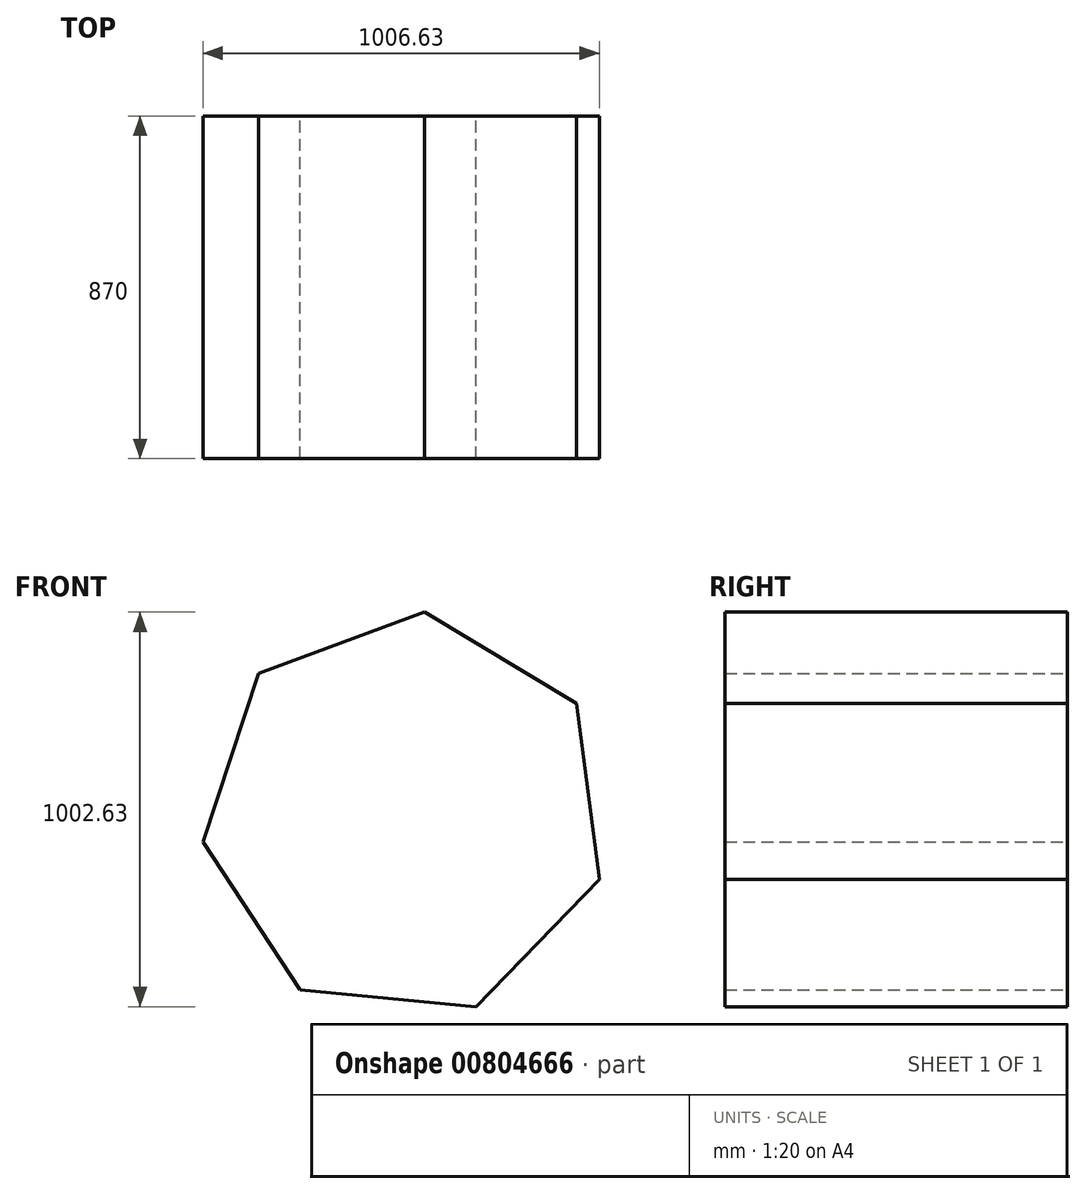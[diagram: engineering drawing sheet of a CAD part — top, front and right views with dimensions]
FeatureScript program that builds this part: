
annotation { "Feature Type Name" : "Feature", "Feature Type Description" : "" }
export const myFeature = defineFeature(function(context is Context, id is Id, definition is map)
    precondition{}
    {
        {
            var Q0;
            Q0=qCreatedBy(makeId("Front.planeOp"),FACE);
            var sketch = newSketch(context, id + "F0", { "sketchPlane" : qUnion([Q0])});
            skCircle(sketch, "E0.cCircle", {"center": v(0, -30.66) * mm, "radius": 467.22 * mm, "construction": true});
            skLineSegment(sketch, "E0.0", {"start": v(48.96, 485.6) * mm, "end": v(434.15, 252.94) * mm});
            skLineSegment(sketch, "E0.1", {"start": v(434.15, 252.94) * mm, "end": v(492.42, -193.28) * mm});
            skLineSegment(sketch, "E0.2", {"start": v(492.42, -193.28) * mm, "end": v(179.88, -517.04) * mm});
            skLineSegment(sketch, "E0.3", {"start": v(179.88, -517.04) * mm, "end": v(-268.11, -474.55) * mm});
            skLineSegment(sketch, "E0.4", {"start": v(-268.11, -474.55) * mm, "end": v(-514.2, -97.8) * mm});
            skLineSegment(sketch, "E0.5", {"start": v(-514.2, -97.8) * mm, "end": v(-373.1, 329.5) * mm});
            skLineSegment(sketch, "E0.6", {"start": v(-373.1, 329.5) * mm, "end": v(48.96, 485.6) * mm});
            skPoint(sketch, "E0.0.midPoint", {"position": v(241.56, 369.27) * mm});
            skSolve(sketch);
        }
        {
            var Q0;
            Q0 = qSketchRegion(id + "F0", true);
            extrude(context, id + "F1", {"entities" : qUnion([Q0]), "depth" : 870 * mm, "offsetDistance" : 25 * mm});
        }
    });
